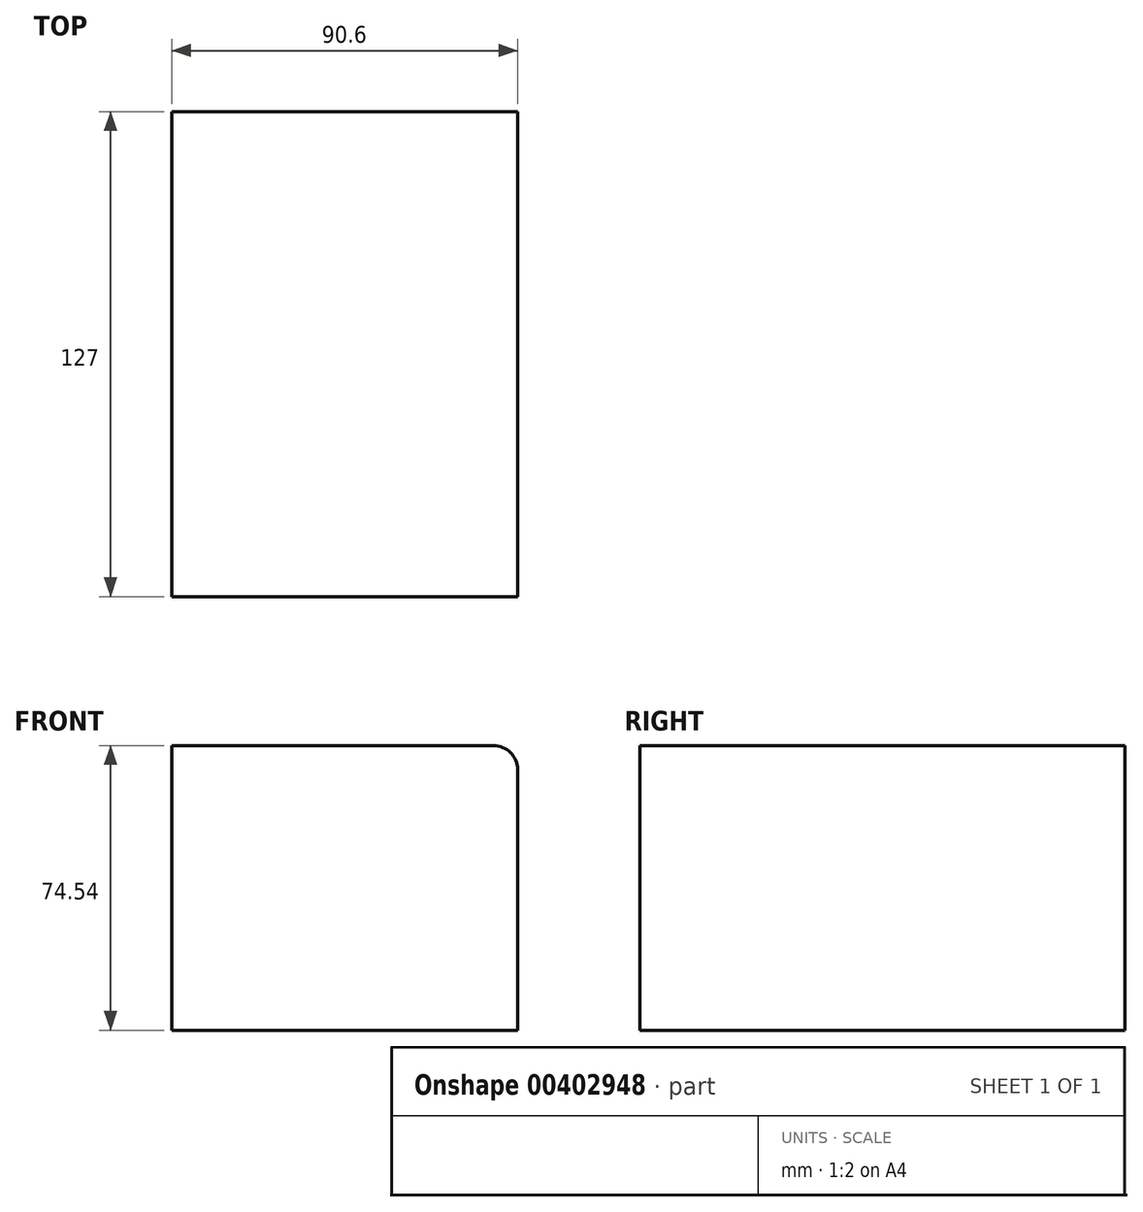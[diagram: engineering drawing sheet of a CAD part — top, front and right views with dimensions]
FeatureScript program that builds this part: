
annotation { "Feature Type Name" : "Feature", "Feature Type Description" : "" }
export const myFeature = defineFeature(function(context is Context, id is Id, definition is map)
    precondition{}
    {
        {
            var Q0;
            Q0=qCreatedBy(makeId("Front.planeOp"),FACE);
            var sketch = newSketch(context, id + "F0", { "sketchPlane" : qUnion([Q0])});
            skLineSegment(sketch, "E0.bottom", {"start": v(-101.07, 50.9) * mm, "end": v(-185.32, 50.9) * mm});
            skLineSegment(sketch, "E0.top", {"start": v(-94.72, -23.64) * mm, "end": v(-185.32, -23.64) * mm});
            skLineSegment(sketch, "E0.left", {"start": v(-94.72, 44.55) * mm, "end": v(-94.72, -23.64) * mm});
            skLineSegment(sketch, "E0.right", {"start": v(-185.32, 50.9) * mm, "end": v(-185.32, -23.64) * mm});
            skPoint(sketch, "E0.middle", {"position": v(-140.02, 13.63) * mm});
            skLineSegment(sketch, "E1", {"start": v(-117.37, 8.85) * mm, "end": v(-117.37, -63.66) * mm});
            skPoint(sketch, "E2.visualSharp", {"position": v(-94.72, 50.9) * mm});
            skArc(sketch, "E2.filletArc", {"start": v(-94.72, 44.55) * mm, "mid": v(-96.58, 49.04) * mm, "end": v(-101.07, 50.9) * mm});
            skSolve(sketch);
        }
        {
            var Q0;
            Q0=makeQuery(id+"F0.imprint","IMPRINT",FACE,{"disambiguationData":[TD([[makeQuery(id+"F0.imprint","IMPRINT",EDGE,{"derivedFrom":sQuery(id+"F0.wireOp",EDGE,"E0.bottom")}),1.0]])]});
            extrude(context, id + "F1", {"entities" : qUnion([Q0]), "depth" : 127 * mm});
        }
    });
